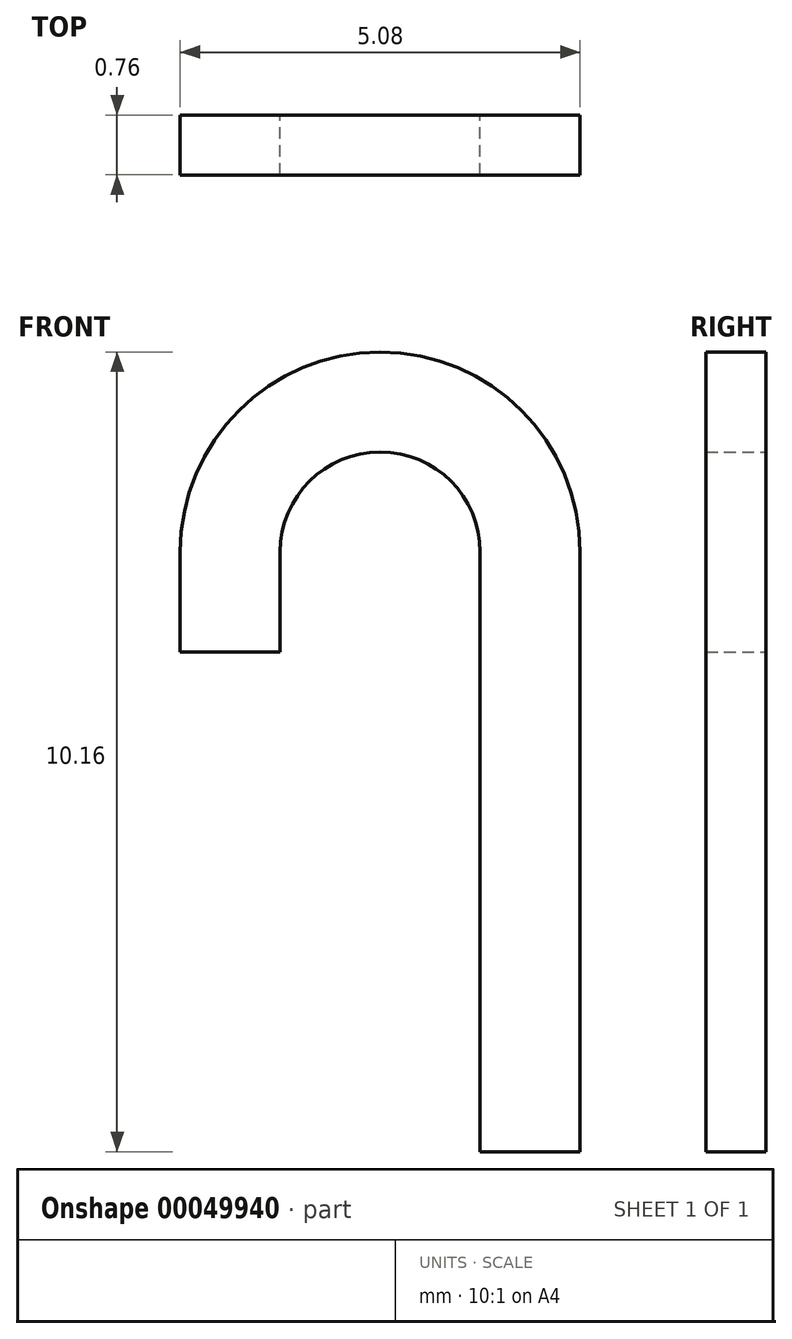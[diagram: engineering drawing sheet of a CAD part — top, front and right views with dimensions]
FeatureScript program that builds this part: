
annotation { "Feature Type Name" : "Feature", "Feature Type Description" : "" }
export const myFeature = defineFeature(function(context is Context, id is Id, definition is map)
    precondition{}
    {
        {
            var Q0;
            Q0=qCreatedBy(makeId("Front.planeOp"),FACE);
            var sketch = newSketch(context, id + "F0", { "sketchPlane" : qUnion([Q0])});
            skLineSegment(sketch, "E0", {"start": v(0, 0) * mm, "end": v(1.27, 0) * mm});
            skLineSegment(sketch, "E1", {"start": v(1.27, 0) * mm, "end": v(1.27, 7.62) * mm});
            skLineSegment(sketch, "E2", {"start": v(0, 0) * mm, "end": v(0, 7.62) * mm});
            skLineSegment(sketch, "E3", {"start": v(0, 7.62) * mm, "end": v(-6.66, 7.62) * mm, "construction": true});
            skLineSegment(sketch, "E4", {"start": v(0, 7.62) * mm, "end": v(-2.54, 7.62) * mm, "construction": true});
            skArc(sketch, "E5", {"start": v(0, 7.62) * mm, "mid": v(-1.27, 8.9) * mm, "end": v(-2.54, 7.62) * mm});
            skArc(sketch, "E6", {"start": v(1.27, 7.62) * mm, "mid": v(-1.27, 10.16) * mm, "end": v(-3.81, 7.62) * mm});
            skLineSegment(sketch, "E7", {"start": v(-3.81, 7.62) * mm, "end": v(-3.81, 6.35) * mm});
            skLineSegment(sketch, "E8", {"start": v(-3.81, 6.35) * mm, "end": v(-2.54, 6.35) * mm});
            skLineSegment(sketch, "E9", {"start": v(-2.54, 7.62) * mm, "end": v(-2.54, 6.35) * mm});
            skSolve(sketch);
        }
        {
            var Q0;
            Q0 = qSketchRegion(id + "F0", true);
            extrude(context, id + "F1", {"entities" : qUnion([Q0]), "depth" : 0.76 * mm});
        }
    });
